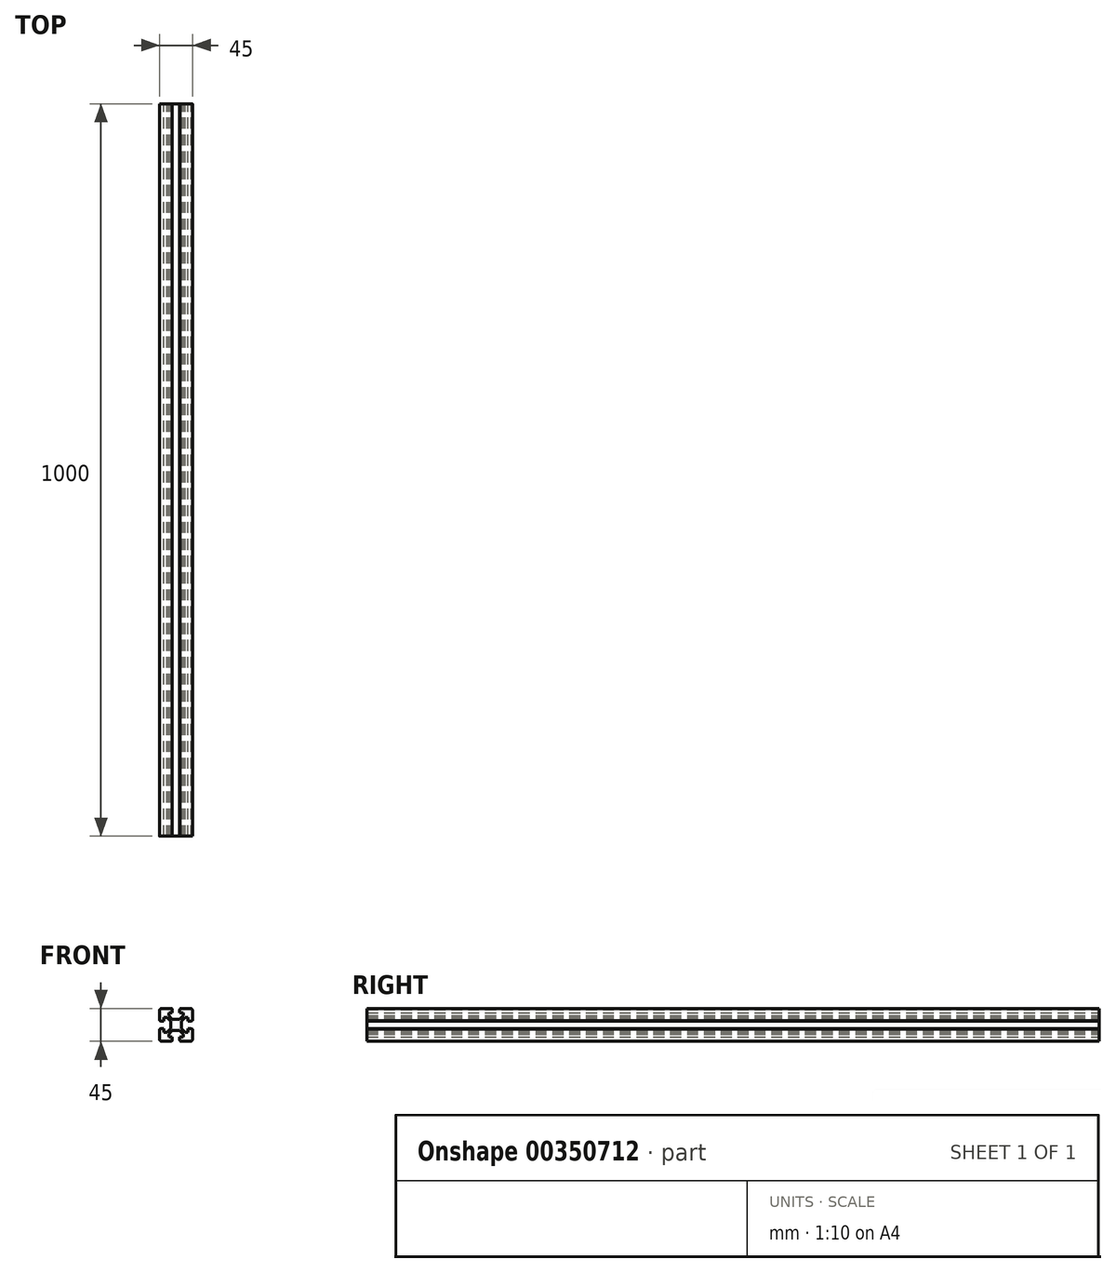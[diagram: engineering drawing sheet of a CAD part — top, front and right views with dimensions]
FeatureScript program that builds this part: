
annotation { "Feature Type Name" : "Feature", "Feature Type Description" : "" }
export const myFeature = defineFeature(function(context is Context, id is Id, definition is map)
    precondition{}
    {
        {
            var Q0;
            Q0=qCreatedBy(makeId("Front.planeOp"),FACE);
            var sketch = newSketch(context, id + "F0", { "sketchPlane" : qUnion([Q0])});
            skLineSegment(sketch, "E0", {"start": v(80.5, 122.5) * mm, "end": v(93.5, 122.5) * mm});
            skLineSegment(sketch, "E1", {"start": v(95, 121) * mm, "end": v(95, 116.5) * mm});
            skLineSegment(sketch, "E2", {"start": v(95, 116.5) * mm, "end": v(90, 116.5) * mm});
            skLineSegment(sketch, "E3", {"start": v(90, 116.5) * mm, "end": v(90, 112.5) * mm});
            skLineSegment(sketch, "E4", {"start": v(90, 112.5) * mm, "end": v(95, 107.5) * mm});
            skLineSegment(sketch, "E5", {"start": v(95, 107.5) * mm, "end": v(100, 107.5) * mm});
            skLineSegment(sketch, "E6", {"start": v(95, 121) * mm, "end": v(94.5, 121) * mm});
            skLineSegment(sketch, "E7", {"start": v(94.5, 121) * mm, "end": v(94.5, 121.5) * mm});
            skPoint(sketch, "E8.orphan", {"position": v(95, 122.5) * mm});
            skPoint(sketch, "E9.visualSharp", {"position": v(94.5, 122.5) * mm});
            skArc(sketch, "E9.filletArc", {"start": v(94.5, 121.5) * mm, "mid": v(94.2, 122.2) * mm, "end": v(93.5, 122.5) * mm});
            skPoint(sketch, "E10.visualSharp", {"position": v(77.5, 122.5) * mm});
            skArc(sketch, "E10.filletArc", {"start": v(80.5, 122.5) * mm, "mid": v(79.35, 122.27) * mm, "end": v(78.38, 121.62) * mm});
            skLineSegment(sketch, "E11.4", {"start": v(-7, 19.5) * mm, "end": v(-7, 19.5) * mm});
            skLineSegment(sketch, "E11.11", {"start": v(-19.5, 7) * mm, "end": v(-19.5, 7) * mm});
            skLineSegment(sketch, "E12", {"start": v(77.5, 122.5) * mm, "end": v(100, 100) * mm, "construction": true});
            skLineSegment(sketch, "E13.MirrorCS", {"start": v(92.5, 105) * mm, "end": v(92.5, 100) * mm});
            skLineSegment(sketch, "E14.MirrorCS", {"start": v(87.5, 110) * mm, "end": v(92.5, 105) * mm});
            skLineSegment(sketch, "E15.MirrorCS", {"start": v(83.5, 110) * mm, "end": v(87.5, 110) * mm});
            skLineSegment(sketch, "E16.MirrorCS", {"start": v(83.5, 105) * mm, "end": v(83.5, 110) * mm});
            skLineSegment(sketch, "E17.MirrorCS", {"start": v(79, 105) * mm, "end": v(83.5, 105) * mm});
            skLineSegment(sketch, "E18.MirrorCS", {"start": v(79, 105) * mm, "end": v(79, 105.5) * mm});
            skLineSegment(sketch, "E19.MirrorCS", {"start": v(79, 105.5) * mm, "end": v(78.5, 105.5) * mm});
            skArc(sketch, "E20.MirrorCS", {"start": v(78.5, 105.5) * mm, "mid": v(77.8, 105.8) * mm, "end": v(77.5, 106.5) * mm});
            skLineSegment(sketch, "E21.MirrorCS", {"start": v(77.5, 119.5) * mm, "end": v(77.5, 106.5) * mm});
            skArc(sketch, "E22.MirrorCS", {"start": v(77.5, 119.5) * mm, "mid": v(77.73, 120.65) * mm, "end": v(78.38, 121.62) * mm});
            skLineSegment(sketch, "E23.MirrorCS", {"start": v(105, 121) * mm, "end": v(105.5, 121) * mm});
            skLineSegment(sketch, "E24.MirrorCS", {"start": v(105.5, 121) * mm, "end": v(105.5, 121.5) * mm});
            skLineSegment(sketch, "E25.MirrorCS", {"start": v(121, 105.5) * mm, "end": v(121.5, 105.5) * mm});
            skLineSegment(sketch, "E26.MirrorCS", {"start": v(121, 105) * mm, "end": v(121, 105.5) * mm});
            skArc(sketch, "E27.MirrorCS", {"start": v(105.5, 121.5) * mm, "mid": v(105.8, 122.2) * mm, "end": v(106.5, 122.5) * mm});
            skLineSegment(sketch, "E28.MirrorCS", {"start": v(110, 116.5) * mm, "end": v(110, 112.5) * mm});
            skArc(sketch, "E29.MirrorCS", {"start": v(122.5, 119.5) * mm, "mid": v(122.27, 120.65) * mm, "end": v(121.62, 121.62) * mm});
            skLineSegment(sketch, "E30.MirrorCS", {"start": v(112.5, 110) * mm, "end": v(107.5, 105) * mm});
            skLineSegment(sketch, "E31.MirrorCS", {"start": v(110, 112.5) * mm, "end": v(105, 107.5) * mm});
            skPoint(sketch, "E32.MirrorP", {"position": v(105.5, 122.5) * mm});
            skLineSegment(sketch, "E33.MirrorCS", {"start": v(105, 116.5) * mm, "end": v(110, 116.5) * mm});
            skArc(sketch, "E34.MirrorCS", {"start": v(119.5, 122.5) * mm, "mid": v(120.65, 122.27) * mm, "end": v(121.62, 121.62) * mm});
            skLineSegment(sketch, "E35.MirrorCS", {"start": v(121, 105) * mm, "end": v(116.5, 105) * mm});
            skLineSegment(sketch, "E36.MirrorCS", {"start": v(122.5, 119.5) * mm, "end": v(122.5, 106.5) * mm});
            skArc(sketch, "E37.MirrorCS", {"start": v(121.5, 105.5) * mm, "mid": v(122.2, 105.8) * mm, "end": v(122.5, 106.5) * mm});
            skLineSegment(sketch, "E38.MirrorCS", {"start": v(107.5, 105) * mm, "end": v(107.5, 100) * mm});
            skLineSegment(sketch, "E39.MirrorCS", {"start": v(116.5, 110) * mm, "end": v(112.5, 110) * mm});
            skPoint(sketch, "E40.MirrorP", {"position": v(122.5, 122.5) * mm});
            skLineSegment(sketch, "E41.MirrorCS", {"start": v(122.5, 122.5) * mm, "end": v(100, 100) * mm, "construction": true});
            skLineSegment(sketch, "E42.MirrorCS", {"start": v(105, 121) * mm, "end": v(105, 116.5) * mm});
            skLineSegment(sketch, "E43.MirrorCS", {"start": v(116.5, 105) * mm, "end": v(116.5, 110) * mm});
            skLineSegment(sketch, "E44.MirrorCS", {"start": v(105, 107.5) * mm, "end": v(100, 107.5) * mm});
            skPoint(sketch, "E45.MirrorP", {"position": v(105, 122.5) * mm});
            skLineSegment(sketch, "E46.MirrorCS", {"start": v(119.5, 122.5) * mm, "end": v(106.5, 122.5) * mm});
            skLineSegment(sketch, "E47.MirrorCS", {"start": v(94.5, 79) * mm, "end": v(94.5, 78.5) * mm});
            skLineSegment(sketch, "E48.MirrorCS", {"start": v(79, 95) * mm, "end": v(79, 94.5) * mm});
            skLineSegment(sketch, "E49.MirrorCS", {"start": v(95, 92.5) * mm, "end": v(100, 92.5) * mm});
            skLineSegment(sketch, "E50.MirrorCS", {"start": v(79, 94.5) * mm, "end": v(78.5, 94.5) * mm});
            skLineSegment(sketch, "E51.MirrorCS", {"start": v(95, 79) * mm, "end": v(94.5, 79) * mm});
            skArc(sketch, "E52.MirrorCS", {"start": v(94.5, 78.5) * mm, "mid": v(94.2, 77.8) * mm, "end": v(93.5, 77.5) * mm});
            skLineSegment(sketch, "E53.MirrorCS", {"start": v(77.5, 80.5) * mm, "end": v(77.5, 93.5) * mm});
            skLineSegment(sketch, "E54.MirrorCS", {"start": v(83.5, 90) * mm, "end": v(87.5, 90) * mm});
            skPoint(sketch, "E55.MirrorP", {"position": v(95, 77.5) * mm});
            skLineSegment(sketch, "E56.MirrorCS", {"start": v(90, 83.5) * mm, "end": v(90, 87.5) * mm});
            skArc(sketch, "E57.MirrorCS", {"start": v(78.5, 94.5) * mm, "mid": v(77.8, 94.2) * mm, "end": v(77.5, 93.5) * mm});
            skLineSegment(sketch, "E58.MirrorCS", {"start": v(80.5, 77.5) * mm, "end": v(93.5, 77.5) * mm});
            skPoint(sketch, "E59.MirrorP", {"position": v(77.5, 77.5) * mm});
            skPoint(sketch, "E60.MirrorP", {"position": v(94.5, 77.5) * mm});
            skLineSegment(sketch, "E61.MirrorCS", {"start": v(87.5, 90) * mm, "end": v(92.5, 95) * mm});
            skLineSegment(sketch, "E62.MirrorCS", {"start": v(90, 87.5) * mm, "end": v(95, 92.5) * mm});
            skLineSegment(sketch, "E63.MirrorCS", {"start": v(95, 79) * mm, "end": v(95, 83.5) * mm});
            skLineSegment(sketch, "E64.MirrorCS", {"start": v(77.5, 77.5) * mm, "end": v(100, 100) * mm, "construction": true});
            skArc(sketch, "E65.MirrorCS", {"start": v(80.5, 77.5) * mm, "mid": v(79.35, 77.73) * mm, "end": v(78.38, 78.38) * mm});
            skArc(sketch, "E66.MirrorCS", {"start": v(77.5, 80.5) * mm, "mid": v(77.73, 79.35) * mm, "end": v(78.38, 78.38) * mm});
            skLineSegment(sketch, "E67.MirrorCS", {"start": v(83.5, 95) * mm, "end": v(83.5, 90) * mm});
            skLineSegment(sketch, "E68.MirrorCS", {"start": v(95, 83.5) * mm, "end": v(90, 83.5) * mm});
            skLineSegment(sketch, "E69.MirrorCS", {"start": v(79, 95) * mm, "end": v(83.5, 95) * mm});
            skLineSegment(sketch, "E70.MirrorCS", {"start": v(121, 95) * mm, "end": v(121, 94.5) * mm});
            skLineSegment(sketch, "E71.MirrorCS", {"start": v(105, 79) * mm, "end": v(105.5, 79) * mm});
            skLineSegment(sketch, "E72.MirrorCS", {"start": v(105.5, 79) * mm, "end": v(105.5, 78.5) * mm});
            skLineSegment(sketch, "E73.MirrorCS", {"start": v(121, 94.5) * mm, "end": v(121.5, 94.5) * mm});
            skArc(sketch, "E74.MirrorCS", {"start": v(105.5, 78.5) * mm, "mid": v(105.8, 77.8) * mm, "end": v(106.5, 77.5) * mm});
            skArc(sketch, "E75.MirrorCS", {"start": v(122.5, 80.5) * mm, "mid": v(122.27, 79.35) * mm, "end": v(121.62, 78.38) * mm});
            skLineSegment(sketch, "E76.MirrorCS", {"start": v(121, 95) * mm, "end": v(116.5, 95) * mm});
            skArc(sketch, "E77.MirrorCS", {"start": v(121.5, 94.5) * mm, "mid": v(122.2, 94.2) * mm, "end": v(122.5, 93.5) * mm});
            skLineSegment(sketch, "E78.MirrorCS", {"start": v(116.5, 90) * mm, "end": v(112.5, 90) * mm});
            skPoint(sketch, "E79.MirrorP", {"position": v(105, 77.5) * mm});
            skPoint(sketch, "E80.MirrorP", {"position": v(105.5, 77.5) * mm});
            skLineSegment(sketch, "E81.MirrorCS", {"start": v(105, 83.5) * mm, "end": v(110, 83.5) * mm});
            skPoint(sketch, "E82.MirrorP", {"position": v(122.5, 77.5) * mm});
            skLineSegment(sketch, "E83.MirrorCS", {"start": v(112.5, 90) * mm, "end": v(107.5, 95) * mm});
            skLineSegment(sketch, "E84.MirrorCS", {"start": v(110, 83.5) * mm, "end": v(110, 87.5) * mm});
            skLineSegment(sketch, "E85.MirrorCS", {"start": v(110, 87.5) * mm, "end": v(105, 92.5) * mm});
            skLineSegment(sketch, "E86.MirrorCS", {"start": v(116.5, 95) * mm, "end": v(116.5, 90) * mm});
            skArc(sketch, "E87.MirrorCS", {"start": v(119.5, 77.5) * mm, "mid": v(120.65, 77.73) * mm, "end": v(121.62, 78.38) * mm});
            skLineSegment(sketch, "E88.MirrorCS", {"start": v(119.5, 77.5) * mm, "end": v(106.5, 77.5) * mm});
            skLineSegment(sketch, "E89.MirrorCS", {"start": v(105, 79) * mm, "end": v(105, 83.5) * mm});
            skLineSegment(sketch, "E90.MirrorCS", {"start": v(122.5, 80.5) * mm, "end": v(122.5, 93.5) * mm});
            skLineSegment(sketch, "E91.MirrorCS", {"start": v(107.5, 95) * mm, "end": v(107.5, 100) * mm});
            skLineSegment(sketch, "E92.MirrorCS", {"start": v(105, 92.5) * mm, "end": v(100, 92.5) * mm});
            skLineSegment(sketch, "E93.MirrorCS", {"start": v(92.5, 95) * mm, "end": v(92.5, 100) * mm});
            skSolve(sketch);
        }
        {
            var Q0;
            Q0=qSketchRegion(id+"F0",true);
            extrude(context, id + "F1", {"entities" : qUnion([Q0]), "depth" : 1000 * mm});
        }
    });
